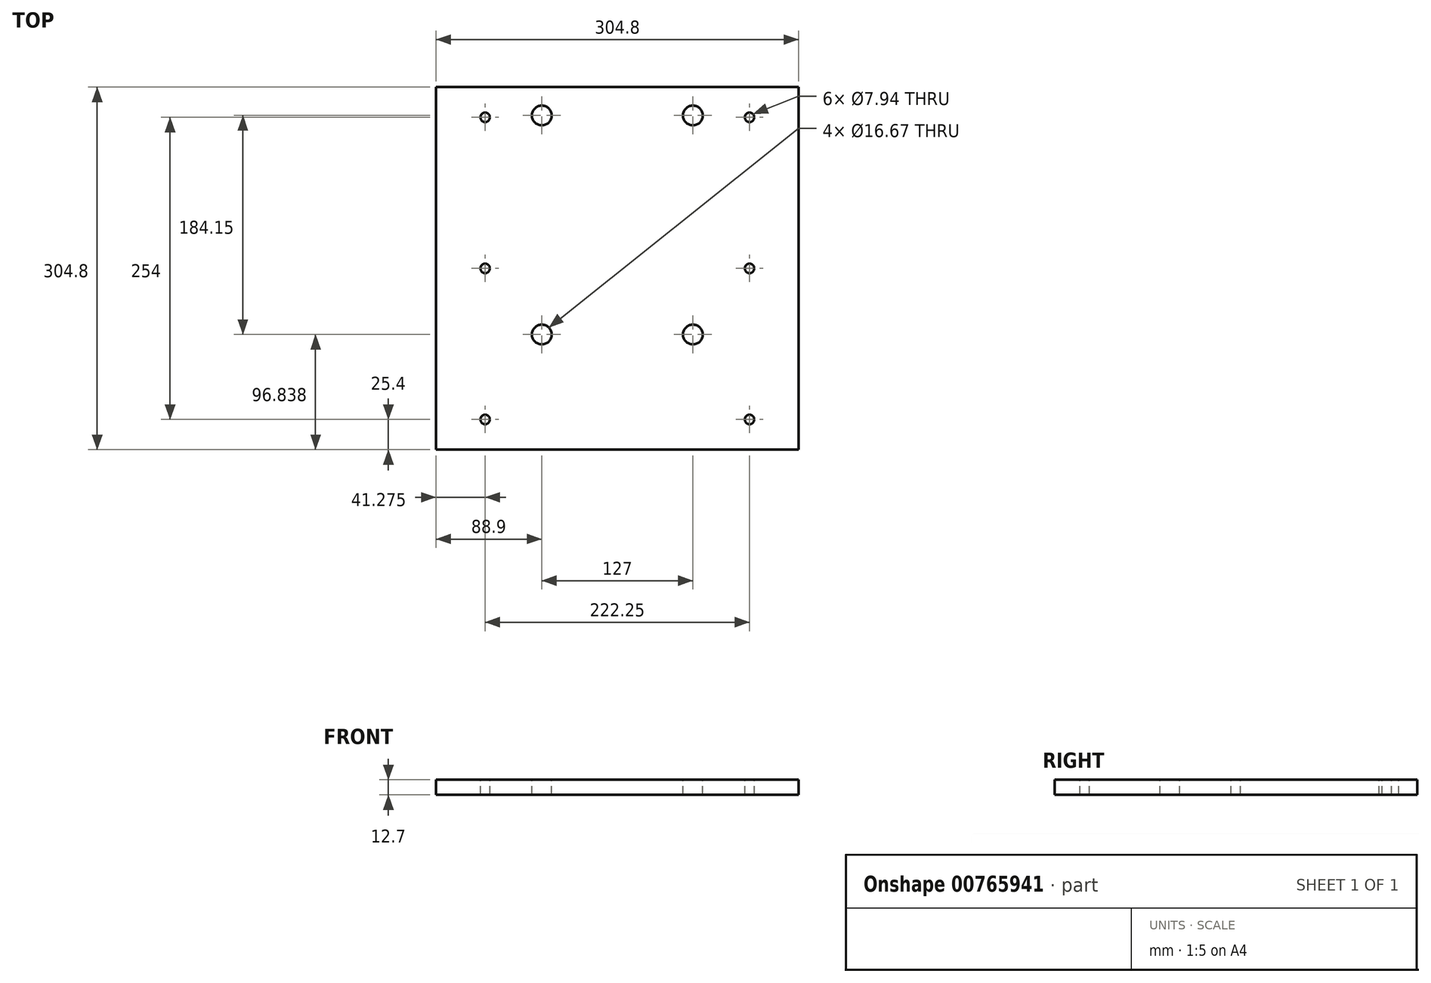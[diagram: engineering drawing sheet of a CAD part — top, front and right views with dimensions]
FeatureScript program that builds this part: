
annotation { "Feature Type Name" : "Feature", "Feature Type Description" : "" }
export const myFeature = defineFeature(function(context is Context, id is Id, definition is map)
    precondition{}
    {
        {
            var Q0;
            Q0=qCreatedBy(makeId("Top.planeOp"),FACE);
            var sketch = newSketch(context, id + "F0", { "sketchPlane" : qUnion([Q0])});
            skLineSegment(sketch, "E0.bottom", {"start": v(0, 0) * mm, "end": v(-304.8, 0) * mm});
            skLineSegment(sketch, "E0.top", {"start": v(0, 304.8) * mm, "end": v(-304.8, 304.8) * mm});
            skLineSegment(sketch, "E0.left", {"start": v(0, 0) * mm, "end": v(0, 304.8) * mm});
            skLineSegment(sketch, "E0.right", {"start": v(-304.8, 0) * mm, "end": v(-304.8, 304.8) * mm});
            skLineSegment(sketch, "E1", {"start": v(-152.4, 304.8) * mm, "end": v(-152.4, 0) * mm, "construction": true});
            skLineSegment(sketch, "E2", {"start": v(-41.28, 304.8) * mm, "end": v(-41.27, 0) * mm, "construction": true});
            skPoint(sketch, "E3", {"position": v(-41.28, 279.4) * mm});
            skLineSegment(sketch, "E4", {"start": v(0, 152.4) * mm, "end": v(-304.8, 152.4) * mm, "construction": true});
            skPoint(sketch, "E5", {"position": v(-41.28, 152.4) * mm});
            skPoint(sketch, "E6.MirrorP", {"position": v(-41.27, 25.4) * mm});
            skLineSegment(sketch, "E7", {"start": v(-88.9, 152.4) * mm, "end": v(-88.9, 304.8) * mm, "construction": true});
            skPoint(sketch, "E8", {"position": v(-88.9, 280.99) * mm});
            skLineSegment(sketch, "E9", {"start": v(-88.9, 228.6) * mm, "end": v(-88.9, 0) * mm, "construction": true});
            skPoint(sketch, "E10", {"position": v(-88.9, 96.84) * mm});
            skPoint(sketch, "E11.MirrorP", {"position": v(-215.9, 280.99) * mm});
            skPoint(sketch, "E12.MirrorP", {"position": v(-215.9, 96.84) * mm});
            skPoint(sketch, "E13.MirrorP", {"position": v(-263.53, 279.4) * mm});
            skPoint(sketch, "E14.MirrorP", {"position": v(-263.53, 152.4) * mm});
            skPoint(sketch, "E15.MirrorP", {"position": v(-263.53, 25.4) * mm});
            skSolve(sketch);
        }
        {
            var Q0;
            Q0 = qSketchRegion(id + "F0", true);
            extrude(context, id + "F1", {"entities" : qUnion([Q0]), "oppositeDirection" : true, "depth" : 12.7 * mm, "offsetDistance" : 25.4 * mm});
        }
        {
            var Q0;
            Q0=sQuery(id+"F0.wireOp",VERTEX,"E13.MirrorP");
            var Q1;
            Q1=sQuery(id+"F0.wireOp",VERTEX,"E14.MirrorP");
            var Q2;
            Q2=sQuery(id+"F0.wireOp",VERTEX,"E15.MirrorP");
            var Q3;
            Q3=sQuery(id+"F0.wireOp",VERTEX,"E3");
            var Q4;
            Q4=sQuery(id+"F0.wireOp",VERTEX,"E5");
            var Q5;
            Q5=sQuery(id+"F0.wireOp",VERTEX,"E6.MirrorP");
            var Q6;
            Q6=makeQuery(id+"F1.opExtrude","SWEPT_BODY",BODY,{"disambiguationData":[OSD([sQuery(id+"F0.wireOp",EDGE,"E0.bottom"),sQuery(id+"F0.wireOp",EDGE,"E0.top"),sQuery(id+"F0.wireOp",EDGE,"E0.left"),sQuery(id+"F0.wireOp",EDGE,"E0.right")])]});
            hole(context, id + "F2", {"style" : HoleStyle.SIMPLE, "endStyle" : HoleEndStyle.BLIND, "standardTappedOrClearance" : lookupTablePath({ "standard" : "ANSI", "engagement" : "75%", "pitch" : "16 tpi", "size" : "3/8", "type" : "Tapped" }), "standardBlindInLast" : lookupTablePath({ "standard" : "ANSI", "engagement" : "75%", "pitch" : "16 tpi", "size" : "3/8", "type" : "Tapped" }), "holeDiameter" : 7.94 * mm, "majorDiameter" : 9.52 * mm, "showTappedDepth" : true, "holeDepth" : 20.66 * mm, "isTappedThrough" : true, "tappedDepth" : 15.9 * mm, "tapClearance" : 3, "locations" : qUnion([Q0, Q1, Q2, Q3, Q4, Q5]), "scope" : qUnion([Q6])});
        }
        {
            var Q0;
            Q0=sQuery(id+"F0.wireOp",VERTEX,"E11.MirrorP");
            var Q1;
            Q1=sQuery(id+"F0.wireOp",VERTEX,"E8");
            var Q2;
            Q2=sQuery(id+"F0.wireOp",VERTEX,"E10");
            var Q3;
            Q3=sQuery(id+"F0.wireOp",VERTEX,"E12.MirrorP");
            var Q4;
            Q4=makeQuery(id+"F1.opExtrude","SWEPT_BODY",BODY,{"disambiguationData":[OSD([sQuery(id+"F0.wireOp",EDGE,"E0.bottom"),sQuery(id+"F0.wireOp",EDGE,"E0.top"),sQuery(id+"F0.wireOp",EDGE,"E0.left"),sQuery(id+"F0.wireOp",EDGE,"E0.right")])]});
            hole(context, id + "F3", {"style" : HoleStyle.SIMPLE, "endStyle" : HoleEndStyle.BLIND, "standardTappedOrClearance" : lookupTablePath({ "standard" : "ANSI", "fit" : "Normal (ASME)", "size" : "5/8", "type" : "Clearance" }), "standardBlindInLast" : lookupTablePath({ "fit" : "Free", "standard" : "ANSI", "size" : "5/8", "type" : "Clearance" }), "holeDiameter" : 16.67 * mm, "majorDiameter" : 9.52 * mm, "holeDepth" : 20.68 * mm, "isTappedThrough" : true, "tappedDepth" : 15.9 * mm, "tapClearance" : 3, "locations" : qUnion([Q0, Q1, Q2, Q3]), "scope" : qUnion([Q4])});
        }
    });
